# Revit family: 0005524
name_source: partatom
category: Lighting Fixtures
revit_build: Autodesk Revit 2017 (Build: 20190507_1515(x64)
units: mm (PartAtom-declared; Revit-internal decimal feet)

## family parameters
Cut with Voids When Loaded = No
Host = Face
Light Source = No
OmniClass Number = 23.80.70.00
OmniClass Title = Lighting
Part Type = Normal
Room Calculation Point = No
Round Connector Dimension = Use Diameter
Shared = No

## types (2) — shared parameters
Apparent Load = 15 VA
Assembly Code = D5020200
AssetType = Fixed
ClassificationName = Uniclass2015
ClassificationValue = EF_70_80
Default Elevation = 1219 mm
DimmingControlOptions = on board dimming
DocumentationLiterature = http://www.sylvania-lighting.com
DurationUnit = hours
ElectricShockClassification = Class I
ExpectedLife = 50000
IfcExportAs = IfcLightFixtureType
IfcExportType = IfcLightFixtureType
ImpactProtectionIndex = IK02
IngressProtection = IP20
InputNominalFrequency = 50/60 Hz
InputVoltage = 220-240 V AC
Keynote = 16500
Lamp = LED
LampColourRenderingIndex = 90
LampColourTemperature = 4000 K
LampMacAdamStep = 3
LampNominalLuminous = 240/720 lm
LampsType = LED
LuminousEfficacy = 48 lm/W
Manufacturer = Feilo Sylvania
ManufacturerName = Feilo Sylvania
Material = aluminium housing, pc polycarbonate diffuser
Material_1_SYL = Body-Sylvania-StartTrackSpot-White
Material_2_SYL = Spacer-Sylvania-StartTrackSpot-Aluminium
Material_3_SYL = <By Category>
Material_4_SYL = <By Category>
ModelNumber = 0005524
NominalDepth = 60 mm
NominalHeight = 261 mm
NominalLength = 60 mm
PowerConsumption = 15 W
Type Image = <None>
URL = http://www.sylvania-lighting.com
Voltage = 230 V
zero-valued in all types: Cost, PowerFactor

## per-type parameters (varying)
| type | Description | Model | ModelReference | Name | TypeHead_SYL | TypeName |
| 0005524 LENZO S 15W 500LM 940 GLB O/B WHITE - WB | LENZO S 15W 500LM 940 GLB O/B WHITE - WB | LENZO S 15W 500LM 940 GLB ON BOARD DIMMING WHITE - WB | LENZO S 15W 500LM 940 GLB ON BOARD DIMMING WHITE - WB | LENZO S 15W 500LM 940 GLB ON BOARD DIMMING WHITE - WB | Lenzo Head : 0005524 LENZO S 15W 500LM 940 GLB O/B WHITE - WB | LENZO S 15W 500LM 940 GLB ON BOARD DIMMING WHITE - WB |
| 0005524 LENZO S 15W 500LM 940 GLB O/B WHITE - NB | LENZO S 15W 500LM 940 GLB O/B WHITE - NB | LENZO S 15W 500LM 940 GLB ON BOARD DIMMING WHITE - NB | LENZO S 15W 500LM 940 GLB ON BOARD DIMMING WHITE - NB | LENZO S 15W 500LM 940 GLB ON BOARD DIMMING WHITE - NB | Lenzo Head : 0005524 LENZO S 15W 500LM 940 GLB O/B WHITE - NB | LENZO S 15W 500LM 940 GLB ON BOARD DIMMING WHITE - NB |

## geometry (parser evidence)
native form markers: Sweep x7
no freeform markers — native parametric forms only
